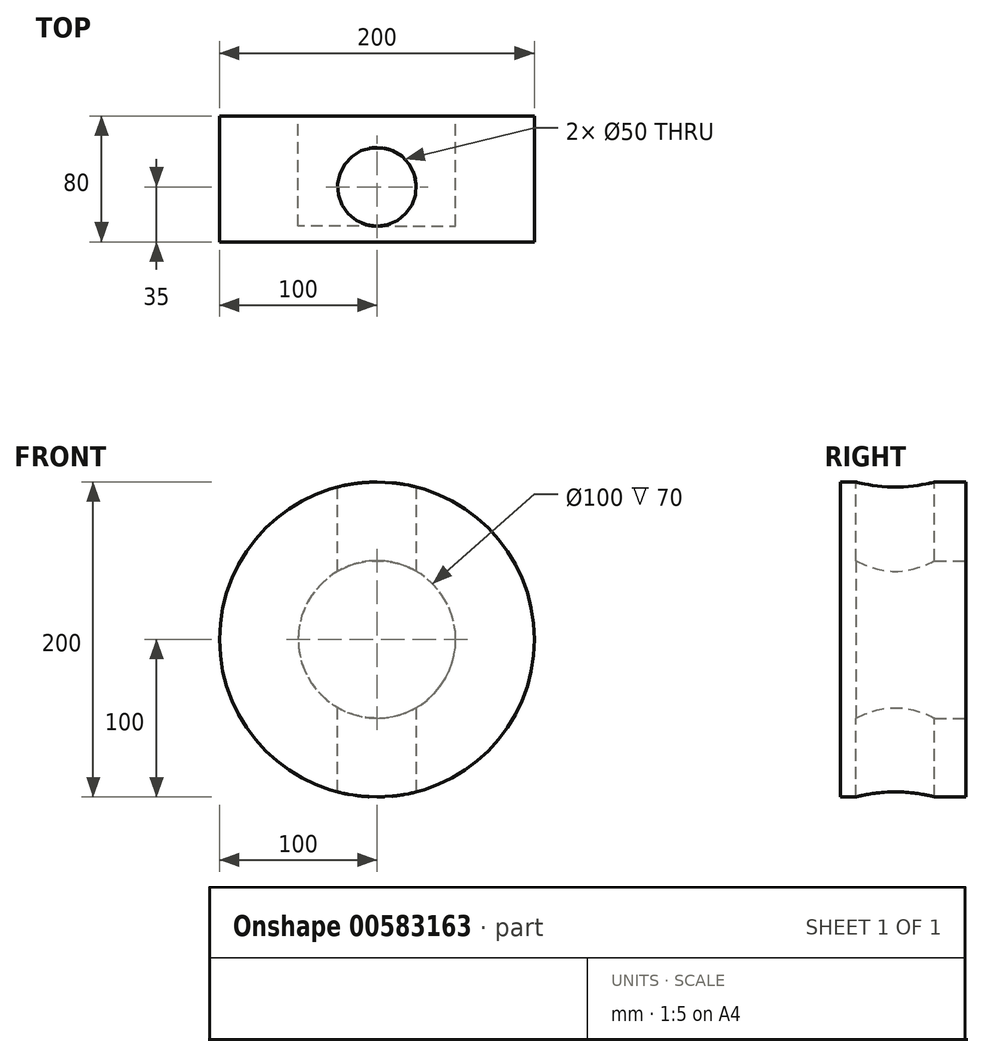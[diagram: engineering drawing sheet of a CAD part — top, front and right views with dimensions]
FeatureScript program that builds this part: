
annotation { "Feature Type Name" : "Feature", "Feature Type Description" : "" }
export const myFeature = defineFeature(function(context is Context, id is Id, definition is map)
    precondition{}
    {
        {
            var Q0;
            Q0=qCreatedBy(makeId("Front.planeOp"),FACE);
            var sketch = newSketch(context, id + "F0", { "sketchPlane" : qUnion([Q0])});
            skCircle(sketch, "E0", {"center": v(0, 0) * mm, "radius": 50 * mm});
            skCircle(sketch, "E1", {"center": v(0, 0) * mm, "radius": 100 * mm});
            skSolve(sketch);
        }
        {
            var Q0;
            Q0 = qSketchRegion(id + "F0", true);
            extrude(context, id + "F1", {"entities" : qUnion([Q0]), "depth" : 70 * mm, "offsetDistance" : 25 * mm});
        }
        {
            var Q0;
            Q0=qCreatedBy(makeId("Top.planeOp"),FACE);
            var sketch = newSketch(context, id + "F2", { "sketchPlane" : qUnion([Q0])});
            skCircle(sketch, "E2", {"center": v(0, -45) * mm, "radius": 25 * mm});
            skSolve(sketch);
        }
        {
            var Q0;
            Q0=makeQuery(id+"F1.opExtrude","CAP_FACE",FACE,{"disambiguationData":[OSD([sQuery(id+"F0.wireOp",EDGE,"E0"),sQuery(id+"F0.wireOp",EDGE,"E1")])],"isStart":false});
            var sketch = newSketch(context, id + "F3", { "sketchPlane" : qUnion([Q0])});
            skCircle(sketch, "E3.0", {"center": v(0, 0) * mm, "radius": 100 * mm});
            skSolve(sketch);
        }
        {
            var Q0;
            Q0 = qSketchRegion(id + "F3", true);
            extrude(context, id + "F4", {"entities" : qUnion([Q0]), "operationType" : NewBodyOperationType.ADD, "depth" : 10 * mm, "offsetDistance" : 25 * mm});
        }
        {
            var Q0;
            Q0 = qSketchRegion(id + "F2", true);
            var Q1;
            Q1=sQuery(id+"F2.wireOp",EDGE,"E2");
            extrude(context, id + "F5", {"entities" : qUnion([Q0]), "operationType" : NewBodyOperationType.REMOVE, "surfaceEntities" : qUnion([Q1]), "endBound" : BoundingType.SYMMETRIC, "oppositeDirection" : true, "depth" : 250 * mm, "offsetDistance" : 25 * mm});
        }
    });
